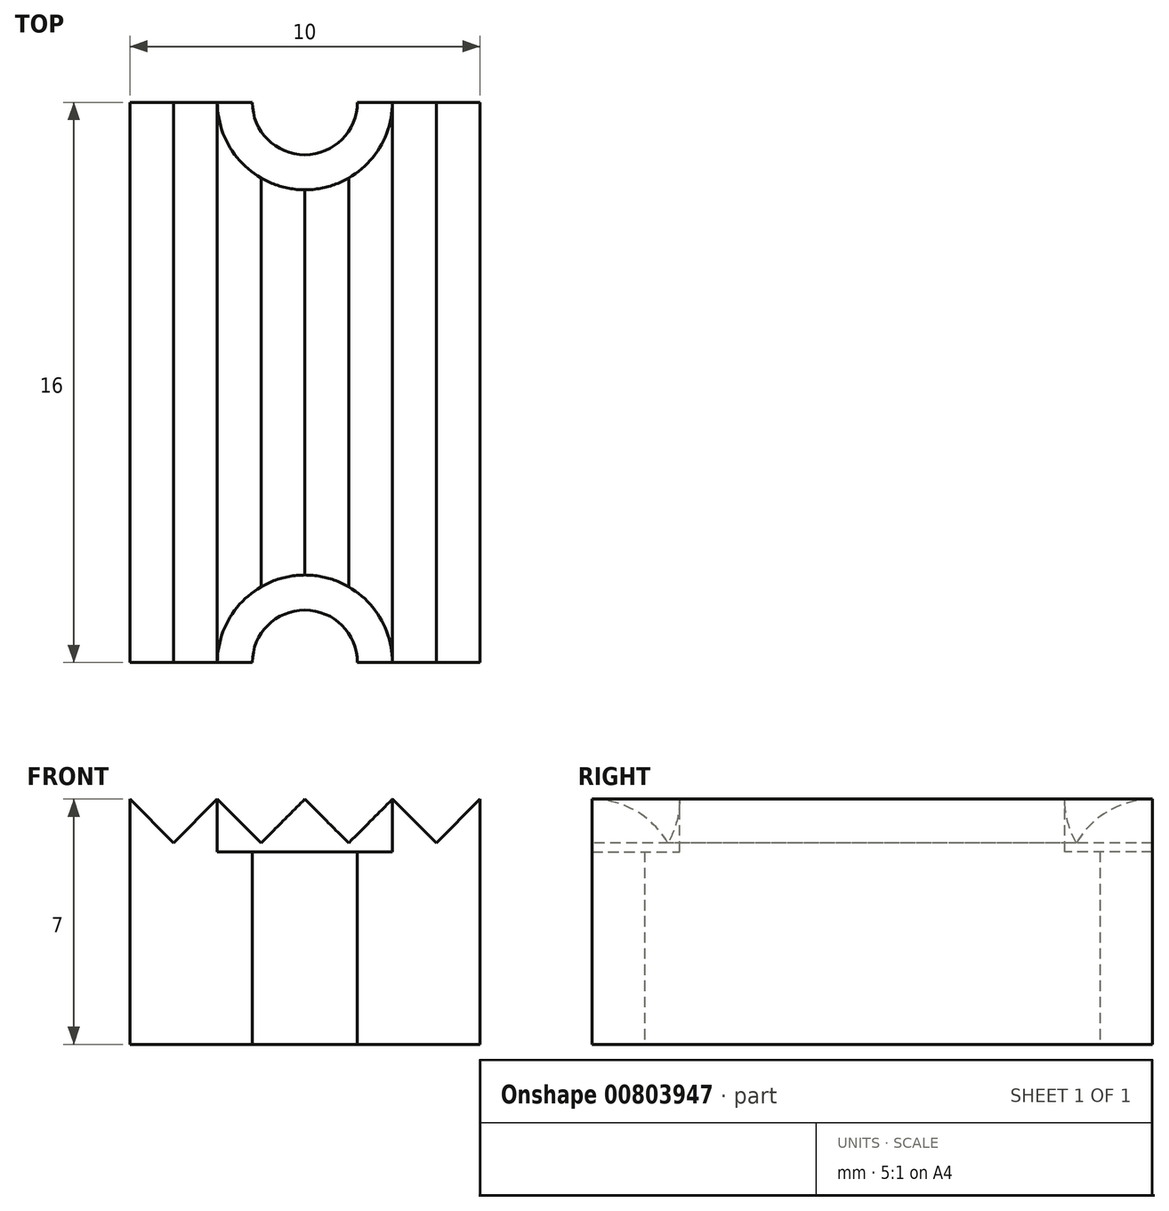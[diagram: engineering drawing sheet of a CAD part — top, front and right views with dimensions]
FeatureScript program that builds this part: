
annotation { "Feature Type Name" : "Feature", "Feature Type Description" : "" }
export const myFeature = defineFeature(function(context is Context, id is Id, definition is map)
    precondition{}
    {
        {
            var Q0;
            Q0=qCreatedBy(makeId("Top.planeOp"),FACE);
            var sketch = newSketch(context, id + "F0", { "sketchPlane" : qUnion([Q0])});
            skPoint(sketch, "E0", {"position": v(0, 8) * mm});
            skPoint(sketch, "E1", {"position": v(0, -8) * mm});
            skLineSegment(sketch, "E2.bottom", {"start": v(-5, 8) * mm, "end": v(5, 8) * mm});
            skLineSegment(sketch, "E2.top", {"start": v(-5, -8) * mm, "end": v(5, -8) * mm});
            skLineSegment(sketch, "E2.left", {"start": v(-5, 8) * mm, "end": v(-5, -8) * mm});
            skLineSegment(sketch, "E2.right", {"start": v(5, 8) * mm, "end": v(5, -8) * mm});
            skPoint(sketch, "E2.middle", {"position": v(0, 0) * mm});
            skArc(sketch, "E3", {"start": v(-5, 8) * mm, "mid": v(0, 13) * mm, "end": v(5, 8) * mm});
            skArc(sketch, "E4", {"start": v(5, -8) * mm, "mid": v(0, -13) * mm, "end": v(-5, -8) * mm});
            skCircle(sketch, "E5", {"center": v(0, 8) * mm, "radius": 1.5 * mm});
            skCircle(sketch, "E6", {"center": v(0, -8) * mm, "radius": 1.5 * mm});
            skSolve(sketch);
        }
        {
            var Q0;
            {var subQ1=sQuery(id+"F0.wireOp",EDGE,"E2.left");Q0=makeQuery(id+"F0.imprint","IMPRINT",FACE,{"disambiguationData":[TD([[makeQuery(id+"F0.imprint","IMPRINT",EDGE,{"derivedFrom":subQ1}),1.0]])]});}
            var Q1;
            {var subQ0=sQuery(id+"F0.wireOp",EDGE,"E3");Q1=makeQuery(id+"F0.imprint","IMPRINT",FACE,{"disambiguationData":[TD([[makeQuery(id+"F0.imprint","IMPRINT",EDGE,{"derivedFrom":subQ0}),-1.0]])]});}
            var Q2;
            {var subQ0=sQuery(id+"F0.wireOp",EDGE,"E4");Q2=makeQuery(id+"F0.imprint","IMPRINT",FACE,{"disambiguationData":[TD([[makeQuery(id+"F0.imprint","IMPRINT",EDGE,{"derivedFrom":subQ0}),-1.0]])]});}
            extrude(context, id + "F1", {"entities" : qUnion([Q0, Q1, Q2]), "depth" : 7 * mm, "offsetDistance" : 25 * mm});
        }
        {
            var Q0;
            Q0=qCreatedBy(makeId("Front.planeOp"),FACE);
            var sketch = newSketch(context, id + "F2", { "sketchPlane" : qUnion([Q0])});
            skLineSegment(sketch, "E7", {"start": v(0, 7) * mm, "end": v(-1.25, 5.75) * mm});
            skLineSegment(sketch, "E8", {"start": v(-1.25, 5.75) * mm, "end": v(-2.5, 7) * mm});
            skLineSegment(sketch, "E9", {"start": v(-2.5, 7) * mm, "end": v(-3.75, 5.75) * mm});
            skLineSegment(sketch, "E10", {"start": v(-3.75, 5.75) * mm, "end": v(-5, 7) * mm});
            skLineSegment(sketch, "E11.MirrorCS", {"start": v(2.5, 7) * mm, "end": v(3.75, 5.75) * mm});
            skLineSegment(sketch, "E12.MirrorCS", {"start": v(3.75, 5.75) * mm, "end": v(5, 7) * mm});
            skLineSegment(sketch, "E13.MirrorCS", {"start": v(1.25, 5.75) * mm, "end": v(2.5, 7) * mm});
            skLineSegment(sketch, "E14.MirrorCS", {"start": v(0, 7) * mm, "end": v(1.25, 5.75) * mm});
            skLineSegment(sketch, "E15", {"start": v(-5, 7) * mm, "end": v(5, 7) * mm});
            skLineSegment(sketch, "E16", {"start": v(-5, 7) * mm, "end": v(-3.75, 5.75) * mm});
            skLineSegment(sketch, "E17", {"start": v(-2.5, 7) * mm, "end": v(-5, 7) * mm});
            skSolve(sketch);
        }
        {
            var Q0;
            {var subQ0=sQuery(id+"F2.wireOp",EDGE,"E9");Q0=makeQuery(id+"F2.imprint","IMPRINT",FACE,{"disambiguationData":[TD([[makeQuery(id+"F2.imprint","IMPRINT",EDGE,{"derivedFrom":subQ0}),-1.0]])]});}
            var Q1;
            {var subQ0=sQuery(id+"F2.wireOp",EDGE,"E7");Q1=makeQuery(id+"F2.imprint","IMPRINT",FACE,{"disambiguationData":[TD([[makeQuery(id+"F2.imprint","IMPRINT",EDGE,{"derivedFrom":subQ0}),-1.0]])]});}
            var Q2;
            {var subQ0=sQuery(id+"F2.wireOp",EDGE,"E13.MirrorCS");Q2=makeQuery(id+"F2.imprint","IMPRINT",FACE,{"disambiguationData":[TD([[makeQuery(id+"F2.imprint","IMPRINT",EDGE,{"derivedFrom":subQ0}),1.0]])]});}
            var Q3;
            {var subQ0=sQuery(id+"F2.wireOp",EDGE,"E11.MirrorCS");Q3=makeQuery(id+"F2.imprint","IMPRINT",FACE,{"disambiguationData":[TD([[makeQuery(id+"F2.imprint","IMPRINT",EDGE,{"derivedFrom":subQ0}),1.0]])]});}
            extrude(context, id + "F3", {"entities" : qUnion([Q0, Q1, Q2, Q3]), "depth" : 50 * mm, "offsetDistance" : 25 * mm});
        }
        {
            var Q0;
            Q0=makeQuery(id+"F3.opExtrude","CAP_FACE",FACE,{"disambiguationData":[OSD([sQuery(id+"F2.wireOp",EDGE,"E9"),sQuery(id+"F2.wireOp",EDGE,"E10"),sQuery(id+"F2.wireOp",EDGE,"E15")])],"isStart":false});
            var Q1;
            Q1=makeQuery(id+"F3.opExtrude","CAP_FACE",FACE,{"disambiguationData":[OSD([sQuery(id+"F2.wireOp",EDGE,"E7"),sQuery(id+"F2.wireOp",EDGE,"E8"),sQuery(id+"F2.wireOp",EDGE,"E15")])],"isStart":false});
            var Q2;
            Q2=makeQuery(id+"F3.opExtrude","CAP_FACE",FACE,{"disambiguationData":[OSD([sQuery(id+"F2.wireOp",EDGE,"E13.MirrorCS"),sQuery(id+"F2.wireOp",EDGE,"E14.MirrorCS"),sQuery(id+"F2.wireOp",EDGE,"E15")])],"isStart":false});
            var Q3;
            Q3=makeQuery(id+"F3.opExtrude","CAP_FACE",FACE,{"disambiguationData":[OSD([sQuery(id+"F2.wireOp",EDGE,"E11.MirrorCS"),sQuery(id+"F2.wireOp",EDGE,"E12.MirrorCS"),sQuery(id+"F2.wireOp",EDGE,"E15")])],"isStart":false});
            extrude(context, id + "F4", {"entities" : qUnion([Q0, Q1, Q2, Q3]), "operationType" : NewBodyOperationType.REMOVE, "oppositeDirection" : true, "depth" : 100 * mm, "offsetDistance" : 25 * mm});
        }
        {
            var Q0;
            Q0=qCreatedBy(makeId("Top.planeOp"),FACE);
            cPlane(context, id + "F5", {"entities" : qUnion([Q0]), "cplaneType" : CPlaneType.OFFSET, "offset" : 7 * mm, "width" : 150 * mm, "height" : 150 * mm});
        }
        {
            var Q0;
            Q0=qCreatedBy(id+"F5.planeOp",FACE);
            var sketch = newSketch(context, id + "F6", { "sketchPlane" : qUnion([Q0])});
            skCircle(sketch, "E18", {"center": v(0, 8) * mm, "radius": 2.5 * mm});
            skCircle(sketch, "E19", {"center": v(0, -8) * mm, "radius": 2.5 * mm});
            skSolve(sketch);
        }
        {
            var Q0;
            Q0=makeQuery(id+"F6.imprint","IMPRINT",FACE,{"disambiguationData":[TD([[makeQuery(id+"F6.imprint","IMPRINT",EDGE,{"derivedFrom":sQuery(id+"F6.wireOp",EDGE,"E19")}),1.0]])]});
            var Q1;
            Q1=makeQuery(id+"F6.imprint","IMPRINT",FACE,{"disambiguationData":[TD([[makeQuery(id+"F6.imprint","IMPRINT",EDGE,{"derivedFrom":sQuery(id+"F6.wireOp",EDGE,"E18")}),1.0]])]});
            extrude(context, id + "F7", {"entities" : qUnion([Q0, Q1]), "operationType" : NewBodyOperationType.REMOVE, "oppositeDirection" : true, "depth" : 1.5 * mm, "offsetDistance" : 25 * mm});
        }
    });
